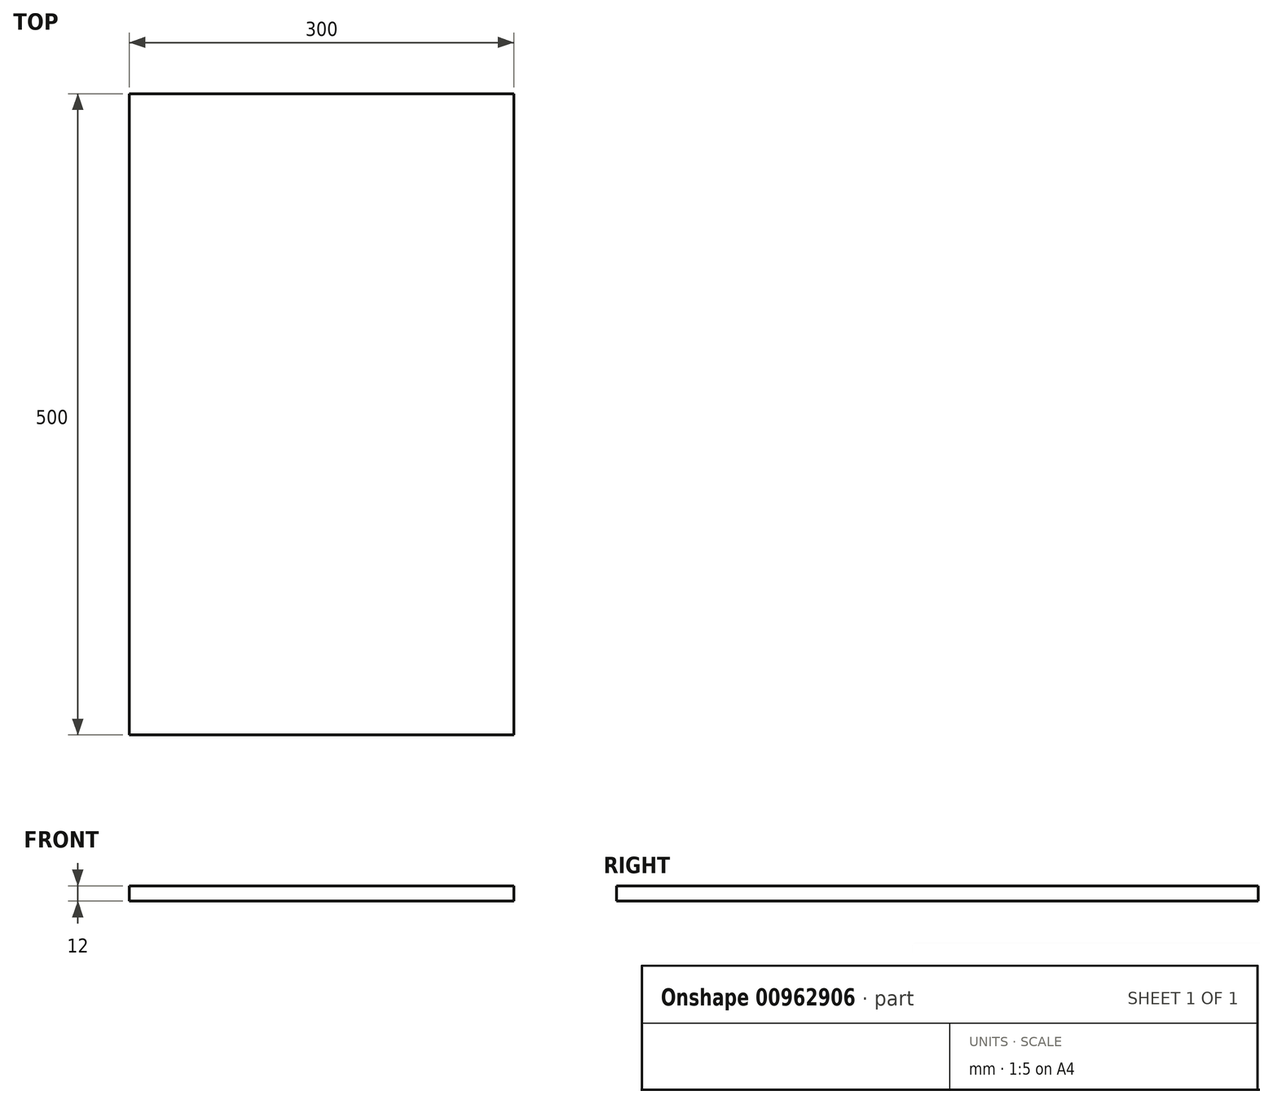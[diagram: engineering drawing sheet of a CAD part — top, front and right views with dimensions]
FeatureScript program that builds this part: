
annotation { "Feature Type Name" : "Feature", "Feature Type Description" : "" }
export const myFeature = defineFeature(function(context is Context, id is Id, definition is map)
    precondition{}
    {
        {
            var Q0;
            Q0=qCreatedBy(makeId("Top.planeOp"),FACE);
            var sketch = newSketch(context, id + "F0", { "sketchPlane" : qUnion([Q0])});
            skLineSegment(sketch, "E0.bottom", {"start": v(-150, 250) * mm, "end": v(150, 250) * mm});
            skLineSegment(sketch, "E0.top", {"start": v(-150, -250) * mm, "end": v(150, -250) * mm});
            skLineSegment(sketch, "E0.left", {"start": v(-150, 250) * mm, "end": v(-150, -250) * mm});
            skLineSegment(sketch, "E0.right", {"start": v(150, 250) * mm, "end": v(150, -250) * mm});
            skPoint(sketch, "E0.middle", {"position": v(0, 0) * mm});
            skSolve(sketch);
        }
        {
            var Q0;
            Q0 = qSketchRegion(id + "F0", true);
            extrude(context, id + "F1", {"entities" : qUnion([Q0]), "depth" : 12 * mm, "offsetDistance" : 25 * mm});
        }
    });
